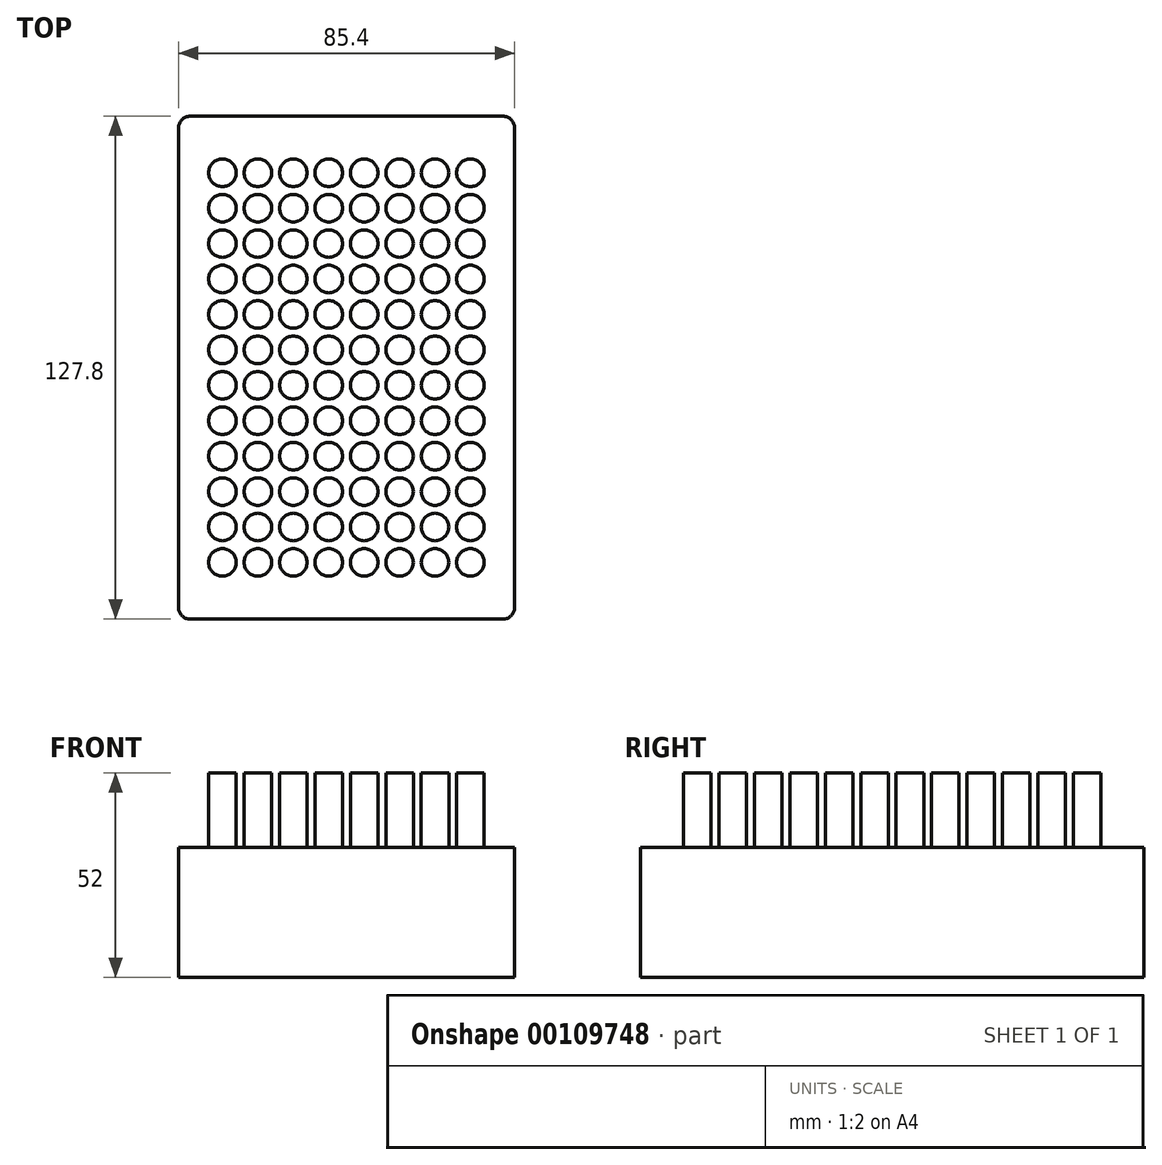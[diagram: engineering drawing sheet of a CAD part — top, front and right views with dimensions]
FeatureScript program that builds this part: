
annotation { "Feature Type Name" : "Feature", "Feature Type Description" : "" }
export const myFeature = defineFeature(function(context is Context, id is Id, definition is map)
    precondition{}
    {
        {
            var Q0;
            Q0=qCreatedBy(makeId("Top.planeOp"),FACE);
            var sketch = newSketch(context, id + "F0", { "sketchPlane" : qUnion([Q0])});
            skLineSegment(sketch, "E0.bottom", {"start": v(42.7, -63.9) * mm, "end": v(-42.7, -63.9) * mm});
            skLineSegment(sketch, "E0.top", {"start": v(42.7, 63.9) * mm, "end": v(-42.7, 63.9) * mm});
            skLineSegment(sketch, "E0.left", {"start": v(42.7, -63.9) * mm, "end": v(42.7, 63.9) * mm});
            skLineSegment(sketch, "E0.right", {"start": v(-42.7, -63.9) * mm, "end": v(-42.7, 63.9) * mm});
            skPoint(sketch, "E0.middle", {"position": v(0, 0) * mm});
            skSolve(sketch);
        }
        {
            var Q0;
            Q0=makeQuery(id+"F0.imprint","IMPRINT",FACE,{"disambiguationData":[TD([[makeQuery(id+"F0.imprint","IMPRINT",EDGE,{"derivedFrom":sQuery(id+"F0.wireOp",EDGE,"E0.bottom")}),-1.0]])]});
            extrude(context, id + "F1", {"entities" : qUnion([Q0]), "depth" : 52 * mm});
        }
        {
            var Q0;
            Q0=makeQuery(id+"F1.opExtrude","CAP_FACE",FACE,{"disambiguationData":[OSD([sQuery(id+"F0.wireOp",EDGE,"E0.bottom"),sQuery(id+"F0.wireOp",EDGE,"E0.top"),sQuery(id+"F0.wireOp",EDGE,"E0.left"),sQuery(id+"F0.wireOp",EDGE,"E0.right")])],"isStart":false});
            var sketch = newSketch(context, id + "F2", { "sketchPlane" : qUnion([Q0])});
            skLineSegment(sketch, "E1", {"start": v(42.7, -63.9) * mm, "end": v(-42.7, -63.9) * mm});
            skLineSegment(sketch, "E2", {"start": v(42.7, -63.9) * mm, "end": v(42.7, 63.9) * mm});
            skLineSegment(sketch, "E3", {"start": v(42.7, 63.9) * mm, "end": v(-42.7, 63.9) * mm});
            skLineSegment(sketch, "E4", {"start": v(-42.7, -63.9) * mm, "end": v(-42.7, 63.9) * mm});
            skCircle(sketch, "E5", {"center": v(-31.54, 49.52) * mm, "radius": 3.5 * mm});
            skCircle(sketch, "E6.1.0.0", {"center": v(-22.54, 49.52) * mm, "radius": 3.5 * mm});
            skCircle(sketch, "E6.2.0.0", {"center": v(-13.54, 49.52) * mm, "radius": 3.5 * mm});
            skCircle(sketch, "E6.3.0.0", {"center": v(-4.54, 49.52) * mm, "radius": 3.5 * mm});
            skCircle(sketch, "E6.4.0.0", {"center": v(4.46, 49.52) * mm, "radius": 3.5 * mm});
            skCircle(sketch, "E6.5.0.0", {"center": v(13.46, 49.52) * mm, "radius": 3.5 * mm});
            skCircle(sketch, "E6.6.0.0", {"center": v(22.46, 49.52) * mm, "radius": 3.5 * mm});
            skCircle(sketch, "E6.7.0.0", {"center": v(31.46, 49.52) * mm, "radius": 3.5 * mm});
            skLineSegment(sketch, "E6.direction1", {"start": v(-31.54, 49.52) * mm, "end": v(-22.54, 49.52) * mm, "construction": true});
            skCircle(sketch, "E7.0.1.0", {"center": v(31.46, 40.52) * mm, "radius": 3.5 * mm});
            skCircle(sketch, "E7.0.1.1", {"center": v(13.46, 40.52) * mm, "radius": 3.5 * mm});
            skCircle(sketch, "E7.0.1.2", {"center": v(-4.54, 40.52) * mm, "radius": 3.5 * mm});
            skCircle(sketch, "E7.0.1.3", {"center": v(22.46, 40.52) * mm, "radius": 3.5 * mm});
            skCircle(sketch, "E7.0.1.4", {"center": v(4.46, 40.52) * mm, "radius": 3.5 * mm});
            skLineSegment(sketch, "E7.0.1.5", {"start": v(-31.54, 40.52) * mm, "end": v(-22.54, 40.52) * mm, "construction": true});
            skCircle(sketch, "E7.0.1.6", {"center": v(-31.54, 40.52) * mm, "radius": 3.5 * mm});
            skCircle(sketch, "E7.0.1.7", {"center": v(-22.54, 40.52) * mm, "radius": 3.5 * mm});
            skCircle(sketch, "E7.0.1.8", {"center": v(-13.54, 40.52) * mm, "radius": 3.5 * mm});
            skCircle(sketch, "E7.0.1.9", {"center": v(-13.54, 40.52) * mm, "radius": 3.5 * mm});
            skCircle(sketch, "E7.0.1.10", {"center": v(-22.54, 40.52) * mm, "radius": 3.5 * mm});
            skCircle(sketch, "E7.0.1.11", {"center": v(31.46, 40.52) * mm, "radius": 3.5 * mm});
            skCircle(sketch, "E7.0.1.12", {"center": v(22.46, 40.52) * mm, "radius": 3.5 * mm});
            skCircle(sketch, "E7.0.1.13", {"center": v(13.46, 40.52) * mm, "radius": 3.5 * mm});
            skCircle(sketch, "E7.0.1.14", {"center": v(4.46, 40.52) * mm, "radius": 3.5 * mm});
            skCircle(sketch, "E7.0.1.15", {"center": v(-4.54, 40.52) * mm, "radius": 3.5 * mm});
            skCircle(sketch, "E7.0.1.16", {"center": v(-31.54, 40.52) * mm, "radius": 3.5 * mm});
            skCircle(sketch, "E7.0.2.0", {"center": v(31.46, 31.52) * mm, "radius": 3.5 * mm});
            skCircle(sketch, "E7.0.2.1", {"center": v(13.46, 31.52) * mm, "radius": 3.5 * mm});
            skCircle(sketch, "E7.0.2.2", {"center": v(-4.54, 31.52) * mm, "radius": 3.5 * mm});
            skCircle(sketch, "E7.0.2.3", {"center": v(22.46, 31.52) * mm, "radius": 3.5 * mm});
            skCircle(sketch, "E7.0.2.4", {"center": v(4.46, 31.52) * mm, "radius": 3.5 * mm});
            skLineSegment(sketch, "E7.0.2.5", {"start": v(-31.54, 31.52) * mm, "end": v(-22.54, 31.52) * mm, "construction": true});
            skCircle(sketch, "E7.0.2.6", {"center": v(-31.54, 31.52) * mm, "radius": 3.5 * mm});
            skCircle(sketch, "E7.0.2.7", {"center": v(-22.54, 31.52) * mm, "radius": 3.5 * mm});
            skCircle(sketch, "E7.0.2.8", {"center": v(-13.54, 31.52) * mm, "radius": 3.5 * mm});
            skCircle(sketch, "E7.0.2.9", {"center": v(-13.54, 31.52) * mm, "radius": 3.5 * mm});
            skCircle(sketch, "E7.0.2.10", {"center": v(-22.54, 31.52) * mm, "radius": 3.5 * mm});
            skCircle(sketch, "E7.0.2.11", {"center": v(31.46, 31.52) * mm, "radius": 3.5 * mm});
            skCircle(sketch, "E7.0.2.12", {"center": v(22.46, 31.52) * mm, "radius": 3.5 * mm});
            skCircle(sketch, "E7.0.2.13", {"center": v(13.46, 31.52) * mm, "radius": 3.5 * mm});
            skCircle(sketch, "E7.0.2.14", {"center": v(4.46, 31.52) * mm, "radius": 3.5 * mm});
            skCircle(sketch, "E7.0.2.15", {"center": v(-4.54, 31.52) * mm, "radius": 3.5 * mm});
            skCircle(sketch, "E7.0.2.16", {"center": v(-31.54, 31.52) * mm, "radius": 3.5 * mm});
            skCircle(sketch, "E7.0.3.0", {"center": v(31.46, 22.52) * mm, "radius": 3.5 * mm});
            skCircle(sketch, "E7.0.3.1", {"center": v(13.46, 22.52) * mm, "radius": 3.5 * mm});
            skCircle(sketch, "E7.0.3.2", {"center": v(-4.54, 22.52) * mm, "radius": 3.5 * mm});
            skCircle(sketch, "E7.0.3.3", {"center": v(22.46, 22.52) * mm, "radius": 3.5 * mm});
            skCircle(sketch, "E7.0.3.4", {"center": v(4.46, 22.52) * mm, "radius": 3.5 * mm});
            skLineSegment(sketch, "E7.0.3.5", {"start": v(-31.54, 22.52) * mm, "end": v(-22.54, 22.52) * mm, "construction": true});
            skCircle(sketch, "E7.0.3.6", {"center": v(-31.54, 22.52) * mm, "radius": 3.5 * mm});
            skCircle(sketch, "E7.0.3.7", {"center": v(-22.54, 22.52) * mm, "radius": 3.5 * mm});
            skCircle(sketch, "E7.0.3.8", {"center": v(-13.54, 22.52) * mm, "radius": 3.5 * mm});
            skCircle(sketch, "E7.0.3.9", {"center": v(-13.54, 22.52) * mm, "radius": 3.5 * mm});
            skCircle(sketch, "E7.0.3.10", {"center": v(-22.54, 22.52) * mm, "radius": 3.5 * mm});
            skCircle(sketch, "E7.0.3.11", {"center": v(31.46, 22.52) * mm, "radius": 3.5 * mm});
            skCircle(sketch, "E7.0.3.12", {"center": v(22.46, 22.52) * mm, "radius": 3.5 * mm});
            skCircle(sketch, "E7.0.3.13", {"center": v(13.46, 22.52) * mm, "radius": 3.5 * mm});
            skCircle(sketch, "E7.0.3.14", {"center": v(4.46, 22.52) * mm, "radius": 3.5 * mm});
            skCircle(sketch, "E7.0.3.15", {"center": v(-4.54, 22.52) * mm, "radius": 3.5 * mm});
            skCircle(sketch, "E7.0.3.16", {"center": v(-31.54, 22.52) * mm, "radius": 3.5 * mm});
            skCircle(sketch, "E7.0.4.0", {"center": v(31.46, 13.52) * mm, "radius": 3.5 * mm});
            skCircle(sketch, "E7.0.4.1", {"center": v(13.46, 13.52) * mm, "radius": 3.5 * mm});
            skCircle(sketch, "E7.0.4.2", {"center": v(-4.54, 13.52) * mm, "radius": 3.5 * mm});
            skCircle(sketch, "E7.0.4.3", {"center": v(22.46, 13.52) * mm, "radius": 3.5 * mm});
            skCircle(sketch, "E7.0.4.4", {"center": v(4.46, 13.52) * mm, "radius": 3.5 * mm});
            skLineSegment(sketch, "E7.0.4.5", {"start": v(-31.54, 13.52) * mm, "end": v(-22.54, 13.52) * mm, "construction": true});
            skCircle(sketch, "E7.0.4.6", {"center": v(-31.54, 13.52) * mm, "radius": 3.5 * mm});
            skCircle(sketch, "E7.0.4.7", {"center": v(-22.54, 13.52) * mm, "radius": 3.5 * mm});
            skCircle(sketch, "E7.0.4.8", {"center": v(-13.54, 13.52) * mm, "radius": 3.5 * mm});
            skCircle(sketch, "E7.0.4.9", {"center": v(-13.54, 13.52) * mm, "radius": 3.5 * mm});
            skCircle(sketch, "E7.0.4.10", {"center": v(-22.54, 13.52) * mm, "radius": 3.5 * mm});
            skCircle(sketch, "E7.0.4.11", {"center": v(31.46, 13.52) * mm, "radius": 3.5 * mm});
            skCircle(sketch, "E7.0.4.12", {"center": v(22.46, 13.52) * mm, "radius": 3.5 * mm});
            skCircle(sketch, "E7.0.4.13", {"center": v(13.46, 13.52) * mm, "radius": 3.5 * mm});
            skCircle(sketch, "E7.0.4.14", {"center": v(4.46, 13.52) * mm, "radius": 3.5 * mm});
            skCircle(sketch, "E7.0.4.15", {"center": v(-4.54, 13.52) * mm, "radius": 3.5 * mm});
            skCircle(sketch, "E7.0.4.16", {"center": v(-31.54, 13.52) * mm, "radius": 3.5 * mm});
            skCircle(sketch, "E7.0.5.0", {"center": v(31.46, 4.52) * mm, "radius": 3.5 * mm});
            skCircle(sketch, "E7.0.5.1", {"center": v(13.46, 4.52) * mm, "radius": 3.5 * mm});
            skCircle(sketch, "E7.0.5.2", {"center": v(-4.54, 4.52) * mm, "radius": 3.5 * mm});
            skCircle(sketch, "E7.0.5.3", {"center": v(22.46, 4.52) * mm, "radius": 3.5 * mm});
            skCircle(sketch, "E7.0.5.4", {"center": v(4.46, 4.52) * mm, "radius": 3.5 * mm});
            skLineSegment(sketch, "E7.0.5.5", {"start": v(-31.54, 4.52) * mm, "end": v(-22.54, 4.52) * mm, "construction": true});
            skCircle(sketch, "E7.0.5.6", {"center": v(-31.54, 4.52) * mm, "radius": 3.5 * mm});
            skCircle(sketch, "E7.0.5.7", {"center": v(-22.54, 4.52) * mm, "radius": 3.5 * mm});
            skCircle(sketch, "E7.0.5.8", {"center": v(-13.54, 4.52) * mm, "radius": 3.5 * mm});
            skCircle(sketch, "E7.0.5.9", {"center": v(-13.54, 4.52) * mm, "radius": 3.5 * mm});
            skCircle(sketch, "E7.0.5.10", {"center": v(-22.54, 4.52) * mm, "radius": 3.5 * mm});
            skCircle(sketch, "E7.0.5.11", {"center": v(31.46, 4.52) * mm, "radius": 3.5 * mm});
            skCircle(sketch, "E7.0.5.12", {"center": v(22.46, 4.52) * mm, "radius": 3.5 * mm});
            skCircle(sketch, "E7.0.5.13", {"center": v(13.46, 4.52) * mm, "radius": 3.5 * mm});
            skCircle(sketch, "E7.0.5.14", {"center": v(4.46, 4.52) * mm, "radius": 3.5 * mm});
            skCircle(sketch, "E7.0.5.15", {"center": v(-4.54, 4.52) * mm, "radius": 3.5 * mm});
            skCircle(sketch, "E7.0.5.16", {"center": v(-31.54, 4.52) * mm, "radius": 3.5 * mm});
            skCircle(sketch, "E7.0.6.0", {"center": v(31.46, -4.48) * mm, "radius": 3.5 * mm});
            skCircle(sketch, "E7.0.6.1", {"center": v(13.46, -4.48) * mm, "radius": 3.5 * mm});
            skCircle(sketch, "E7.0.6.2", {"center": v(-4.54, -4.48) * mm, "radius": 3.5 * mm});
            skCircle(sketch, "E7.0.6.3", {"center": v(22.46, -4.48) * mm, "radius": 3.5 * mm});
            skCircle(sketch, "E7.0.6.4", {"center": v(4.46, -4.48) * mm, "radius": 3.5 * mm});
            skLineSegment(sketch, "E7.0.6.5", {"start": v(-31.54, -4.48) * mm, "end": v(-22.54, -4.48) * mm, "construction": true});
            skCircle(sketch, "E7.0.6.6", {"center": v(-31.54, -4.48) * mm, "radius": 3.5 * mm});
            skCircle(sketch, "E7.0.6.7", {"center": v(-22.54, -4.48) * mm, "radius": 3.5 * mm});
            skCircle(sketch, "E7.0.6.8", {"center": v(-13.54, -4.48) * mm, "radius": 3.5 * mm});
            skCircle(sketch, "E7.0.6.9", {"center": v(-13.54, -4.48) * mm, "radius": 3.5 * mm});
            skCircle(sketch, "E7.0.6.10", {"center": v(-22.54, -4.48) * mm, "radius": 3.5 * mm});
            skCircle(sketch, "E7.0.6.11", {"center": v(31.46, -4.48) * mm, "radius": 3.5 * mm});
            skCircle(sketch, "E7.0.6.12", {"center": v(22.46, -4.48) * mm, "radius": 3.5 * mm});
            skCircle(sketch, "E7.0.6.13", {"center": v(13.46, -4.48) * mm, "radius": 3.5 * mm});
            skCircle(sketch, "E7.0.6.14", {"center": v(4.46, -4.48) * mm, "radius": 3.5 * mm});
            skCircle(sketch, "E7.0.6.15", {"center": v(-4.54, -4.48) * mm, "radius": 3.5 * mm});
            skCircle(sketch, "E7.0.6.16", {"center": v(-31.54, -4.48) * mm, "radius": 3.5 * mm});
            skCircle(sketch, "E7.0.7.0", {"center": v(31.46, -13.48) * mm, "radius": 3.5 * mm});
            skCircle(sketch, "E7.0.7.1", {"center": v(13.46, -13.48) * mm, "radius": 3.5 * mm});
            skCircle(sketch, "E7.0.7.2", {"center": v(-4.54, -13.48) * mm, "radius": 3.5 * mm});
            skCircle(sketch, "E7.0.7.3", {"center": v(22.46, -13.48) * mm, "radius": 3.5 * mm});
            skCircle(sketch, "E7.0.7.4", {"center": v(4.46, -13.48) * mm, "radius": 3.5 * mm});
            skLineSegment(sketch, "E7.0.7.5", {"start": v(-31.54, -13.48) * mm, "end": v(-22.54, -13.48) * mm, "construction": true});
            skCircle(sketch, "E7.0.7.6", {"center": v(-31.54, -13.48) * mm, "radius": 3.5 * mm});
            skCircle(sketch, "E7.0.7.7", {"center": v(-22.54, -13.48) * mm, "radius": 3.5 * mm});
            skCircle(sketch, "E7.0.7.8", {"center": v(-13.54, -13.48) * mm, "radius": 3.5 * mm});
            skCircle(sketch, "E7.0.7.9", {"center": v(-13.54, -13.48) * mm, "radius": 3.5 * mm});
            skCircle(sketch, "E7.0.7.10", {"center": v(-22.54, -13.48) * mm, "radius": 3.5 * mm});
            skCircle(sketch, "E7.0.7.11", {"center": v(31.46, -13.48) * mm, "radius": 3.5 * mm});
            skCircle(sketch, "E7.0.7.12", {"center": v(22.46, -13.48) * mm, "radius": 3.5 * mm});
            skCircle(sketch, "E7.0.7.13", {"center": v(13.46, -13.48) * mm, "radius": 3.5 * mm});
            skCircle(sketch, "E7.0.7.14", {"center": v(4.46, -13.48) * mm, "radius": 3.5 * mm});
            skCircle(sketch, "E7.0.7.15", {"center": v(-4.54, -13.48) * mm, "radius": 3.5 * mm});
            skCircle(sketch, "E7.0.7.16", {"center": v(-31.54, -13.48) * mm, "radius": 3.5 * mm});
            skCircle(sketch, "E7.0.8.0", {"center": v(31.46, -22.48) * mm, "radius": 3.5 * mm});
            skCircle(sketch, "E7.0.8.1", {"center": v(13.46, -22.48) * mm, "radius": 3.5 * mm});
            skCircle(sketch, "E7.0.8.2", {"center": v(-4.54, -22.48) * mm, "radius": 3.5 * mm});
            skCircle(sketch, "E7.0.8.3", {"center": v(22.46, -22.48) * mm, "radius": 3.5 * mm});
            skCircle(sketch, "E7.0.8.4", {"center": v(4.46, -22.48) * mm, "radius": 3.5 * mm});
            skLineSegment(sketch, "E7.0.8.5", {"start": v(-31.54, -22.48) * mm, "end": v(-22.54, -22.48) * mm, "construction": true});
            skCircle(sketch, "E7.0.8.6", {"center": v(-31.54, -22.48) * mm, "radius": 3.5 * mm});
            skCircle(sketch, "E7.0.8.7", {"center": v(-22.54, -22.48) * mm, "radius": 3.5 * mm});
            skCircle(sketch, "E7.0.8.8", {"center": v(-13.54, -22.48) * mm, "radius": 3.5 * mm});
            skCircle(sketch, "E7.0.8.9", {"center": v(-13.54, -22.48) * mm, "radius": 3.5 * mm});
            skCircle(sketch, "E7.0.8.10", {"center": v(-22.54, -22.48) * mm, "radius": 3.5 * mm});
            skCircle(sketch, "E7.0.8.11", {"center": v(31.46, -22.48) * mm, "radius": 3.5 * mm});
            skCircle(sketch, "E7.0.8.12", {"center": v(22.46, -22.48) * mm, "radius": 3.5 * mm});
            skCircle(sketch, "E7.0.8.13", {"center": v(13.46, -22.48) * mm, "radius": 3.5 * mm});
            skCircle(sketch, "E7.0.8.14", {"center": v(4.46, -22.48) * mm, "radius": 3.5 * mm});
            skCircle(sketch, "E7.0.8.15", {"center": v(-4.54, -22.48) * mm, "radius": 3.5 * mm});
            skCircle(sketch, "E7.0.8.16", {"center": v(-31.54, -22.48) * mm, "radius": 3.5 * mm});
            skCircle(sketch, "E7.0.9.0", {"center": v(31.46, -31.48) * mm, "radius": 3.5 * mm});
            skCircle(sketch, "E7.0.9.1", {"center": v(13.46, -31.48) * mm, "radius": 3.5 * mm});
            skCircle(sketch, "E7.0.9.2", {"center": v(-4.54, -31.48) * mm, "radius": 3.5 * mm});
            skCircle(sketch, "E7.0.9.3", {"center": v(22.46, -31.48) * mm, "radius": 3.5 * mm});
            skCircle(sketch, "E7.0.9.4", {"center": v(4.46, -31.48) * mm, "radius": 3.5 * mm});
            skLineSegment(sketch, "E7.0.9.5", {"start": v(-31.54, -31.48) * mm, "end": v(-22.54, -31.48) * mm, "construction": true});
            skCircle(sketch, "E7.0.9.6", {"center": v(-31.54, -31.48) * mm, "radius": 3.5 * mm});
            skCircle(sketch, "E7.0.9.7", {"center": v(-22.54, -31.48) * mm, "radius": 3.5 * mm});
            skCircle(sketch, "E7.0.9.8", {"center": v(-13.54, -31.48) * mm, "radius": 3.5 * mm});
            skCircle(sketch, "E7.0.9.9", {"center": v(-13.54, -31.48) * mm, "radius": 3.5 * mm});
            skCircle(sketch, "E7.0.9.10", {"center": v(-22.54, -31.48) * mm, "radius": 3.5 * mm});
            skCircle(sketch, "E7.0.9.11", {"center": v(31.46, -31.48) * mm, "radius": 3.5 * mm});
            skCircle(sketch, "E7.0.9.12", {"center": v(22.46, -31.48) * mm, "radius": 3.5 * mm});
            skCircle(sketch, "E7.0.9.13", {"center": v(13.46, -31.48) * mm, "radius": 3.5 * mm});
            skCircle(sketch, "E7.0.9.14", {"center": v(4.46, -31.48) * mm, "radius": 3.5 * mm});
            skCircle(sketch, "E7.0.9.15", {"center": v(-4.54, -31.48) * mm, "radius": 3.5 * mm});
            skCircle(sketch, "E7.0.9.16", {"center": v(-31.54, -31.48) * mm, "radius": 3.5 * mm});
            skCircle(sketch, "E7.0.10.0", {"center": v(31.46, -40.48) * mm, "radius": 3.5 * mm});
            skCircle(sketch, "E7.0.10.1", {"center": v(13.46, -40.48) * mm, "radius": 3.5 * mm});
            skCircle(sketch, "E7.0.10.2", {"center": v(-4.54, -40.48) * mm, "radius": 3.5 * mm});
            skCircle(sketch, "E7.0.10.3", {"center": v(22.46, -40.48) * mm, "radius": 3.5 * mm});
            skCircle(sketch, "E7.0.10.4", {"center": v(4.46, -40.48) * mm, "radius": 3.5 * mm});
            skLineSegment(sketch, "E7.0.10.5", {"start": v(-31.54, -40.48) * mm, "end": v(-22.54, -40.48) * mm, "construction": true});
            skCircle(sketch, "E7.0.10.6", {"center": v(-31.54, -40.48) * mm, "radius": 3.5 * mm});
            skCircle(sketch, "E7.0.10.7", {"center": v(-22.54, -40.48) * mm, "radius": 3.5 * mm});
            skCircle(sketch, "E7.0.10.8", {"center": v(-13.54, -40.48) * mm, "radius": 3.5 * mm});
            skCircle(sketch, "E7.0.10.9", {"center": v(-13.54, -40.48) * mm, "radius": 3.5 * mm});
            skCircle(sketch, "E7.0.10.10", {"center": v(-22.54, -40.48) * mm, "radius": 3.5 * mm});
            skCircle(sketch, "E7.0.10.11", {"center": v(31.46, -40.48) * mm, "radius": 3.5 * mm});
            skCircle(sketch, "E7.0.10.12", {"center": v(22.46, -40.48) * mm, "radius": 3.5 * mm});
            skCircle(sketch, "E7.0.10.13", {"center": v(13.46, -40.48) * mm, "radius": 3.5 * mm});
            skCircle(sketch, "E7.0.10.14", {"center": v(4.46, -40.48) * mm, "radius": 3.5 * mm});
            skCircle(sketch, "E7.0.10.15", {"center": v(-4.54, -40.48) * mm, "radius": 3.5 * mm});
            skCircle(sketch, "E7.0.10.16", {"center": v(-31.54, -40.48) * mm, "radius": 3.5 * mm});
            skCircle(sketch, "E7.0.11.0", {"center": v(31.46, -49.48) * mm, "radius": 3.5 * mm});
            skCircle(sketch, "E7.0.11.1", {"center": v(13.46, -49.48) * mm, "radius": 3.5 * mm});
            skCircle(sketch, "E7.0.11.2", {"center": v(-4.54, -49.48) * mm, "radius": 3.5 * mm});
            skCircle(sketch, "E7.0.11.3", {"center": v(22.46, -49.48) * mm, "radius": 3.5 * mm});
            skCircle(sketch, "E7.0.11.4", {"center": v(4.46, -49.48) * mm, "radius": 3.5 * mm});
            skLineSegment(sketch, "E7.0.11.5", {"start": v(-31.54, -49.48) * mm, "end": v(-22.54, -49.48) * mm, "construction": true});
            skCircle(sketch, "E7.0.11.6", {"center": v(-31.54, -49.48) * mm, "radius": 3.5 * mm});
            skCircle(sketch, "E7.0.11.7", {"center": v(-22.54, -49.48) * mm, "radius": 3.5 * mm});
            skCircle(sketch, "E7.0.11.8", {"center": v(-13.54, -49.48) * mm, "radius": 3.5 * mm});
            skCircle(sketch, "E7.0.11.9", {"center": v(-13.54, -49.48) * mm, "radius": 3.5 * mm});
            skCircle(sketch, "E7.0.11.10", {"center": v(-22.54, -49.48) * mm, "radius": 3.5 * mm});
            skCircle(sketch, "E7.0.11.11", {"center": v(31.46, -49.48) * mm, "radius": 3.5 * mm});
            skCircle(sketch, "E7.0.11.12", {"center": v(22.46, -49.48) * mm, "radius": 3.5 * mm});
            skCircle(sketch, "E7.0.11.13", {"center": v(13.46, -49.48) * mm, "radius": 3.5 * mm});
            skCircle(sketch, "E7.0.11.14", {"center": v(4.46, -49.48) * mm, "radius": 3.5 * mm});
            skCircle(sketch, "E7.0.11.15", {"center": v(-4.54, -49.48) * mm, "radius": 3.5 * mm});
            skCircle(sketch, "E7.0.11.16", {"center": v(-31.54, -49.48) * mm, "radius": 3.5 * mm});
            skLineSegment(sketch, "E7.direction1", {"start": v(-31.54, 49.52) * mm, "end": v(-7.53, 49.52) * mm, "construction": true});
            skLineSegment(sketch, "E7.direction2", {"start": v(-31.54, 49.52) * mm, "end": v(-31.54, 40.52) * mm, "construction": true});
            skSolve(sketch);
        }
        {
            var Q0;
            Q0 = qSketchRegion(id + "F2", true);
            extrude(context, id + "F3", {"entities" : qUnion([Q0]), "operationType" : NewBodyOperationType.REMOVE, "oppositeDirection" : true, "depth" : (52 - 33) * mm});
        }
        {
            var Q0;
            Q0=makeQuery(id+"F1.opExtrude","SWEPT_EDGE",EDGE,{"disambiguationData":[OSD([sQuery(id+"F0.wireOp",EDGE,"E0.top"),sQuery(id+"F0.wireOp",EDGE,"E0.right")])]});
            var Q1;
            Q1=makeQuery(id+"F1.opExtrude","SWEPT_EDGE",EDGE,{"disambiguationData":[OSD([sQuery(id+"F0.wireOp",EDGE,"E0.bottom"),sQuery(id+"F0.wireOp",EDGE,"E0.right")])]});
            var Q2;
            Q2=makeQuery(id+"F1.opExtrude","SWEPT_EDGE",EDGE,{"disambiguationData":[OSD([sQuery(id+"F0.wireOp",EDGE,"E0.bottom"),sQuery(id+"F0.wireOp",EDGE,"E0.left")])]});
            var Q3;
            Q3=makeQuery(id+"F1.opExtrude","SWEPT_EDGE",EDGE,{"disambiguationData":[OSD([sQuery(id+"F0.wireOp",EDGE,"E0.top"),sQuery(id+"F0.wireOp",EDGE,"E0.left")])]});
            fillet(context, id + "F4", {"entities" : qUnion([Q0, Q1, Q2, Q3]), "radius" : 3 * mm, "tangentPropagation" : true, "allowEdgeOverflow" : false});
        }
    });
